# Revit family: Specialty Equipment_Hand Dryer_Metlam_EcoJet
name_source: partatom
category: Specialty Equipment
revit_build: Autodesk Revit 2014 (Build: 20130308_1515(x64)
units: mm (PartAtom-declared; Revit-internal decimal feet)

## types (2) — shared parameters
Assembly Code = C1030200
Manufacturer = Metlam
Manufacturer_Overall Depth = 100 mm  [stored 0.328084 ft]
Manufacturer_Overall Height = 216 mm  [stored 0.708661 ft]
Manufacturer_Overall Width = 276 mm  [stored 0.905512 ft]
Manufacturer_URL_Home Page = http://www.metlam.com.au
Manufacturer_URL__Product Specific = http://metlam.com.au
ModifiedIssue_ANZRS = 20151029 $
Type Comments = Hand Dryers
URL = http://www.metlam.com.au

## per-type parameters (varying)
| type | Description | Dryer Material | Manufacturer_Spec Code | Model |
| White PC (276w x 216h x 100d) | Slimline Auto Hand Dryer | z_Metlam_White Powder Coat | EcoSlender-01 | EcoSlender-01 |
| SS (276w x 216h x 100d) | Slimline Eco Auto Operation Hand Dryer | z_Metlam_Stainless Steel | EcoSlender-05-SS | EcoSlender-05-SS |

note: [stored X ft] marks values corroborated as IEEE doubles in the binary element streams (Revit-internal decimal feet)

## geometry (parser evidence)
native form markers: Sweep x1
no freeform markers — native parametric forms only
